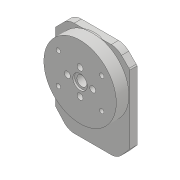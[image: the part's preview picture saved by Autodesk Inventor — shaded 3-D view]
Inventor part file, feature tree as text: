
AUTODESK INVENTOR PART (.ipt)
format: ipt  version: 2018 (Build 220112000, 112)  size: 220,160 bytes
history: native  units: mm
features: sketch x8, extrude x6, other x4, hole x2, pattern_circular x2, fillet x2, projected_geometry x2, plane x1, reference x1
ambient origin geometry x8: Origin, YZ Plane, XZ Plane, XY Plane, X Axis, Y Axis, Z Axis, Center Point
bodies: Solid1 (feature_tree)
feature tree (28):
  extrude  "Extrusion1"  Depth=7.0mm TaperAngle=0.0deg
  extrude  "Extrusion2"  Depth=4.0mm TaperAngle=0.0deg
  hole  "Hole1"  [1 undecoded]
  pattern_circular  "Circular Pattern1"  [2 undecoded]
  extrude  "Extrusion3"  Depth=7.75mm TaperAngle=0.0deg
  extrude  "Extrusion4"  Depth=40.0mm TaperAngle=360.0deg
  extrude  "Extrusion5"  Depth=17.0mm
  pattern_circular  "Circular Pattern2"  [2 undecoded]
  hole  "Hole2"  [1 undecoded]
  fillet  "Fillet1"  Radius=5.0mm
  sketch  "Sketch10"  dims[d21=1.0mm d22=0.0mm d23=6.0mm d24=7.75mm d25=0.0mm d26=40.0mm d27=360.0deg d29=17.0mm d30=24.0mm d31=5.0mm d32=5.0mm d33=2.0mm d34=2.459mm d35=6.0mm d36=9.4mm d37=2.0mm d38=90.0deg d39=8.8mm d40=20.594885mm d43=1.25mm d44=10.0mm d45=0.0mm d46=2.0mm]
  plane  "Work Plane1"
  extrude  "Extrusion7"  Depth=2.0mm
  fillet  "Fillet2"  Radius=1.25mm
  sketch  "Sketch1"  dims[d0=40.0mm d1=7.0mm d2=0.0mm]
  sketch  "Sketch2"  dims[d3=80.4mm d4=4.0mm d5=0.0mm]
  sketch  "Sketch3"  dims[d6=7.0mm]
  sketch  "Sketch4"  dims[d7=3.3mm d8=6.35mm d9=6.3mm d10=2.0mm d11=90.0deg d12=8.0mm d13=20.594885mm d14=40.0mm d15=360.0deg]
  sketch  "Sketch5"  dims[d17=5.5mm]
  sketch  "Sketch6"  dims[d18=10.0mm d19=0.0mm]
  projected_geometry  "Projected Loop1"
  sketch  "Sketch8"  dims[d20=8.0mm]
  projected_geometry  "Projected Loop3"
  reference  "Reference3"
  parser-record x1  (decoder bookkeeping rows leaked as tree rows — omitted from the tree; the rows remain in map.json)
  other  "servocheck.iam"
  other  "bottomarm:1"
  other  "arm1:1"
note: 6 required parameter values undecoded (feature->parameter linkage not recoverable at this tier; creation-order binding heuristic only, values carry confidence <= 0.55)
note: 1 file-system path scrubbed to <path> (originals preserved in map.json)
